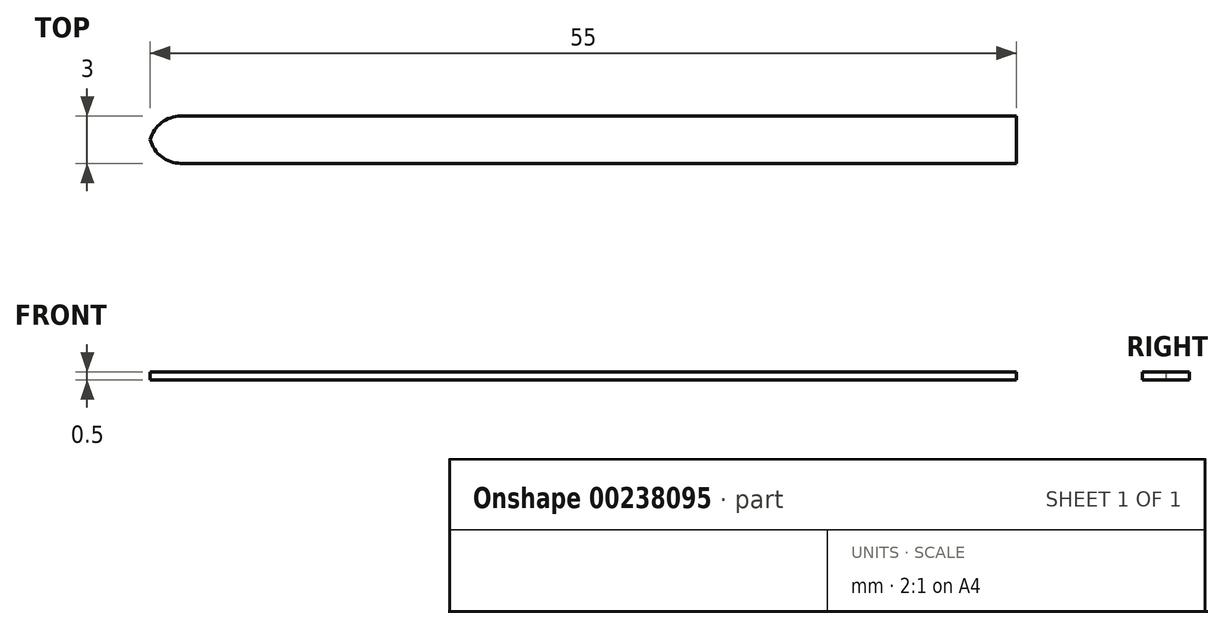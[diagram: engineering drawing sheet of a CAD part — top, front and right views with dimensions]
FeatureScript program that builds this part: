
annotation { "Feature Type Name" : "Feature", "Feature Type Description" : "" }
export const myFeature = defineFeature(function(context is Context, id is Id, definition is map)
    precondition{}
    {
        {
            var Q0;
            Q0=qCreatedBy(makeId("Top.planeOp"),FACE);
            var sketch = newSketch(context, id + "F0", { "sketchPlane" : qUnion([Q0])});
            skLineSegment(sketch, "E0.bottom", {"start": v(27.5, 1.5) * mm, "end": v(-25.56, 1.5) * mm});
            skLineSegment(sketch, "E0.top", {"start": v(27.5, -1.5) * mm, "end": v(-25.56, -1.5) * mm});
            skLineSegment(sketch, "E0.left", {"start": v(27.5, 1.5) * mm, "end": v(27.5, -1.5) * mm});
            skPoint(sketch, "E0.middle", {"position": v(0, 0) * mm});
            skPoint(sketch, "E1.visualSharp", {"position": v(-27.5, 1.5) * mm});
            skArc(sketch, "E1.filletArc", {"start": v(-25.56, 1.5) * mm, "mid": v(-26.79, 1.08) * mm, "end": v(-27.5, 0) * mm});
            skPoint(sketch, "E2.visualSharp", {"position": v(-27.5, -1.5) * mm});
            skArc(sketch, "E2.filletArc", {"start": v(-27.5, 0) * mm, "mid": v(-26.79, -1.08) * mm, "end": v(-25.56, -1.5) * mm});
            skSolve(sketch);
        }
        {
            var Q0;
            Q0 = qSketchRegion(id + "F0", true);
            extrude(context, id + "F1", {"entities" : qUnion([Q0]), "depth" : .5 * mm});
        }
    });
